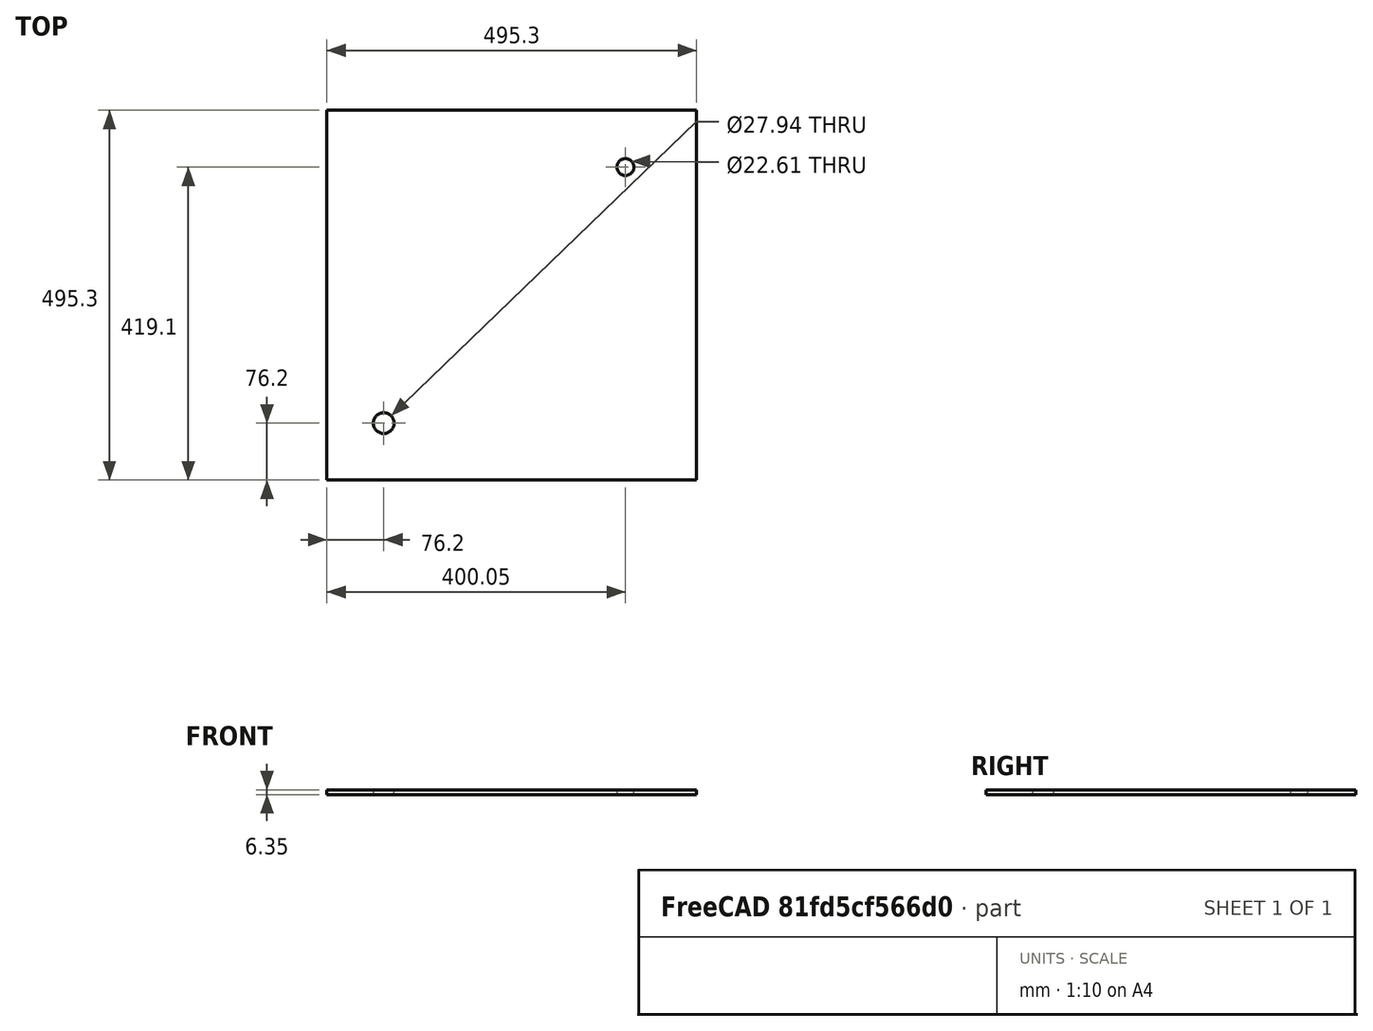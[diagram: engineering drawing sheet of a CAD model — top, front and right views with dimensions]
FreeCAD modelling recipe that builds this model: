
FCSTD DOCUMENT  (FreeCAD 0.16R6712 (Git))
Label: PC_1708_Frame_Tank_inner_side
License: CreativeCommons Attribution
LicenseURL: http://creativecommons.org/licenses/by/4.0/
objects: Sketcher::SketchObject×1, PartDesign::Pad×1
note: 3 computed .brp shape members not serialized (recipe doc carries the construction recipe); baked Part::Feature solids carry a one-line shape summary decoded from their .brp

FEATURE [Sketcher::SketchObject] Sketch
  Placement = pos=(-304.8,-304.8,6.35) rot=(0,0,1;0rad)
  sketch-geometry (14):
    g0: Circle CenterX=152.4 CenterY=171.45 CenterZ=0 NormalX=0 NormalY=0 NormalZ=1 Radius=11.303
    g1: LineSegment [constr] StartX=-38.8567 StartY=228.6 StartZ=0 EndX=9.64244 EndY=228.6 EndZ=0
    g2: LineSegment [constr] StartX=155.973 StartY=228.6 StartZ=0 EndX=204.472 EndY=228.6 EndZ=0
    g3: LineSegment [constr] StartX=152.4 StartY=171.45 StartZ=0 EndX=103.901 EndY=171.45 EndZ=0
    g4: LineSegment StartX=-247.65 StartY=247.65 StartZ=0 EndX=247.65 EndY=247.65 EndZ=0
    g5: LineSegment StartX=247.65 StartY=247.65 StartZ=0 EndX=247.65 EndY=-247.65 EndZ=0
    g6: LineSegment StartX=247.65 StartY=-247.65 StartZ=0 EndX=-247.65 EndY=-247.65 EndZ=0
    g7: LineSegment StartX=-247.65 StartY=-247.65 StartZ=0 EndX=-247.65 EndY=247.65 EndZ=0
    g8: LineSegment [constr] StartX=-26.777 StartY=203.2 StartZ=0 EndX=101.501 EndY=203.2 EndZ=0
    g9: LineSegment [constr] StartX=125.623 StartY=203.2 StartZ=0 EndX=253.901 EndY=203.2 EndZ=0
    g10: Circle CenterX=-171.45 CenterY=-171.45 CenterZ=0 NormalX=0 NormalY=0 NormalZ=1 Radius=13.97
    g11: LineSegment [constr] StartX=-171.45 StartY=-171.45 StartZ=0 EndX=-41.45 EndY=-171.45 EndZ=0
    g12: LineSegment [constr] StartX=-54.194 StartY=-228.6 StartZ=0 EndX=75.806 EndY=-228.6 EndZ=0
    g13: LineSegment [constr] StartX=76.594 StartY=-228.6 StartZ=0 EndX=206.594 EndY=-228.6 EndZ=0
  constraints (32):
    c: Radius(g0) = 11.303
    c: Horizontal(g2)
    c: Horizontal(g1)
    c: Coincident(g3,g0)
    c: Horizontal(g3)
    c: Equal(g2,g1)
    c: Equal(g1,g3)
    c: Coincident(g4,g5)
    c: Coincident(g5,g6)
    c: Coincident(g6,g7)
    c: Coincident(g7,g4)
    c: Horizontal(g4)
    c: Horizontal(g6)
    c: Vertical(g5)
    c: Vertical(g7)
    c: Equal(g5,g6)
    c: DistanceY(g5,g5) = 495.3
    c: Symmetric(g5,g6,g-2)
    c: Symmetric(g5,g4,g-1)
    c: Horizontal(g8)
    c: Horizontal(g9)
    c: Radius(g10) = 13.97
    c: Coincident(g10,g11)
    c: Equal(g11,g12)
    c: Equal(g11,g13)
    c: DistanceY(g6,g10) = 76.2
    c: Horizontal(g11)
    c: Horizontal(g12)
    c: Horizontal(g13)
    c: DistanceX(g6,g10) = 76.2
    c: DistanceY(g0,g4) = 76.2
    c: DistanceX(g0,g-1) = -152.4
FEATURE [PartDesign::Pad] Pad
  Length = 6.35
  Length2 = 100
  Placement = pos=(-304.8,-304.8,6.35) rot=(0,0,1;0rad)
  Sketch = -> Sketch
  Type = 0
